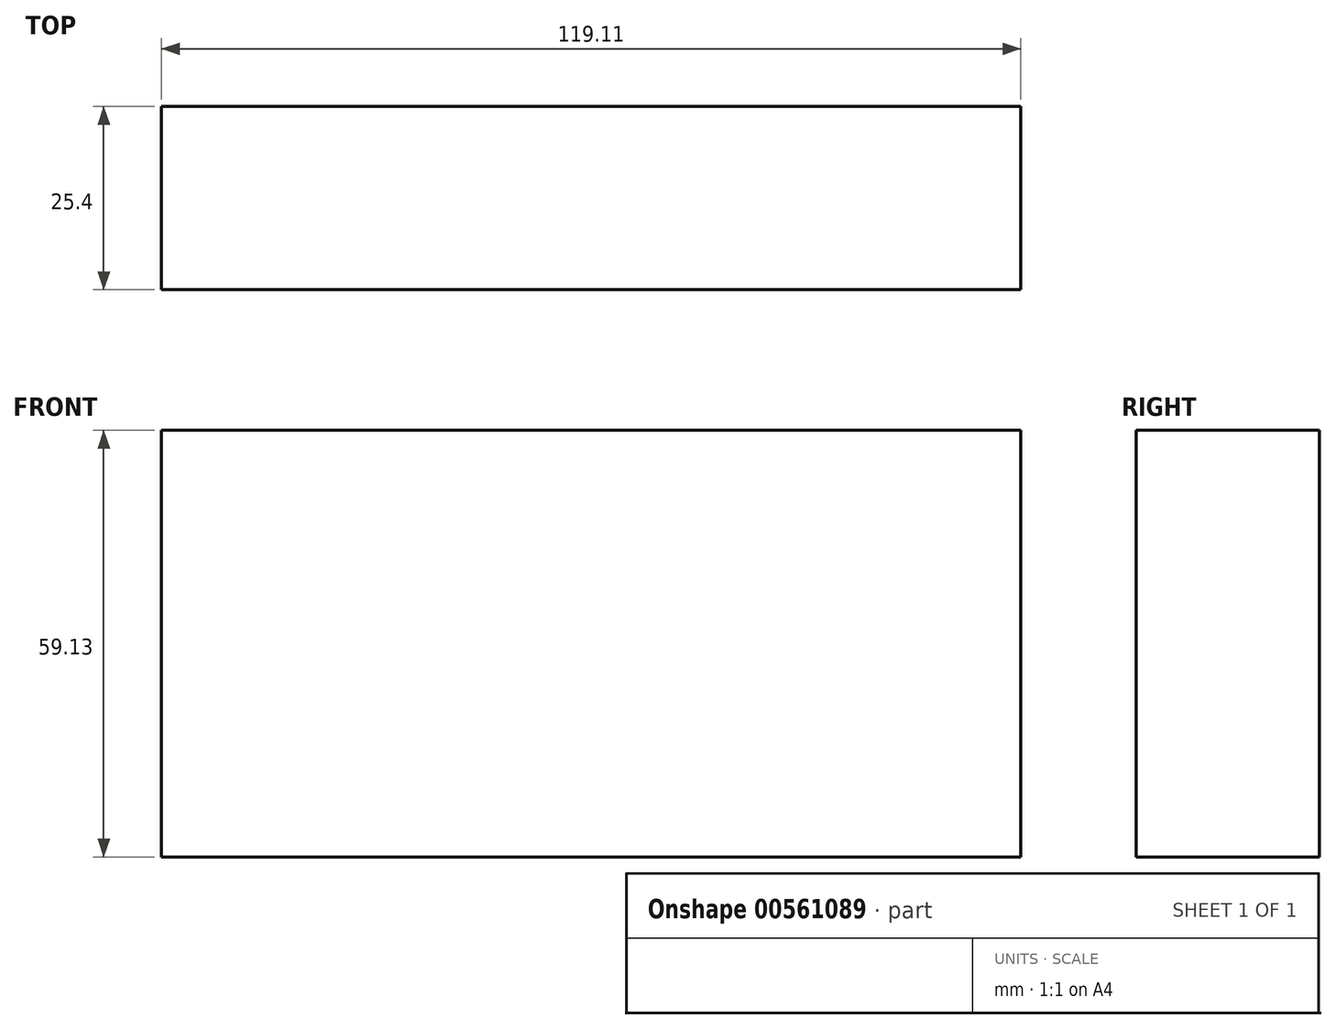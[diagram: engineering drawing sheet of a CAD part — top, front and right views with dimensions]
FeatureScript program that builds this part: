
annotation { "Feature Type Name" : "Feature", "Feature Type Description" : "" }
export const myFeature = defineFeature(function(context is Context, id is Id, definition is map)
    precondition{}
    {
        {
            var Q0;
            Q0=qCreatedBy(makeId("Front.planeOp"),FACE);
            var sketch = newSketch(context, id + "F0", { "sketchPlane" : qUnion([Q0])});
            skLineSegment(sketch, "E0.bottom", {"start": v(-57.93, 26.11) * mm, "end": v(61.18, 26.11) * mm});
            skLineSegment(sketch, "E0.top", {"start": v(-57.93, -33.02) * mm, "end": v(61.18, -33.02) * mm});
            skLineSegment(sketch, "E0.left", {"start": v(-57.93, 26.11) * mm, "end": v(-57.93, -33.02) * mm});
            skLineSegment(sketch, "E0.right", {"start": v(61.18, 26.11) * mm, "end": v(61.18, -33.02) * mm});
            skSolve(sketch);
        }
        {
            var Q0;
            Q0 = qSketchRegion(id + "F0", true);
            extrude(context, id + "F1", {"entities" : qUnion([Q0]), "depth" : 25.4 * mm, "offsetDistance" : 25.4 * mm});
        }
    });
